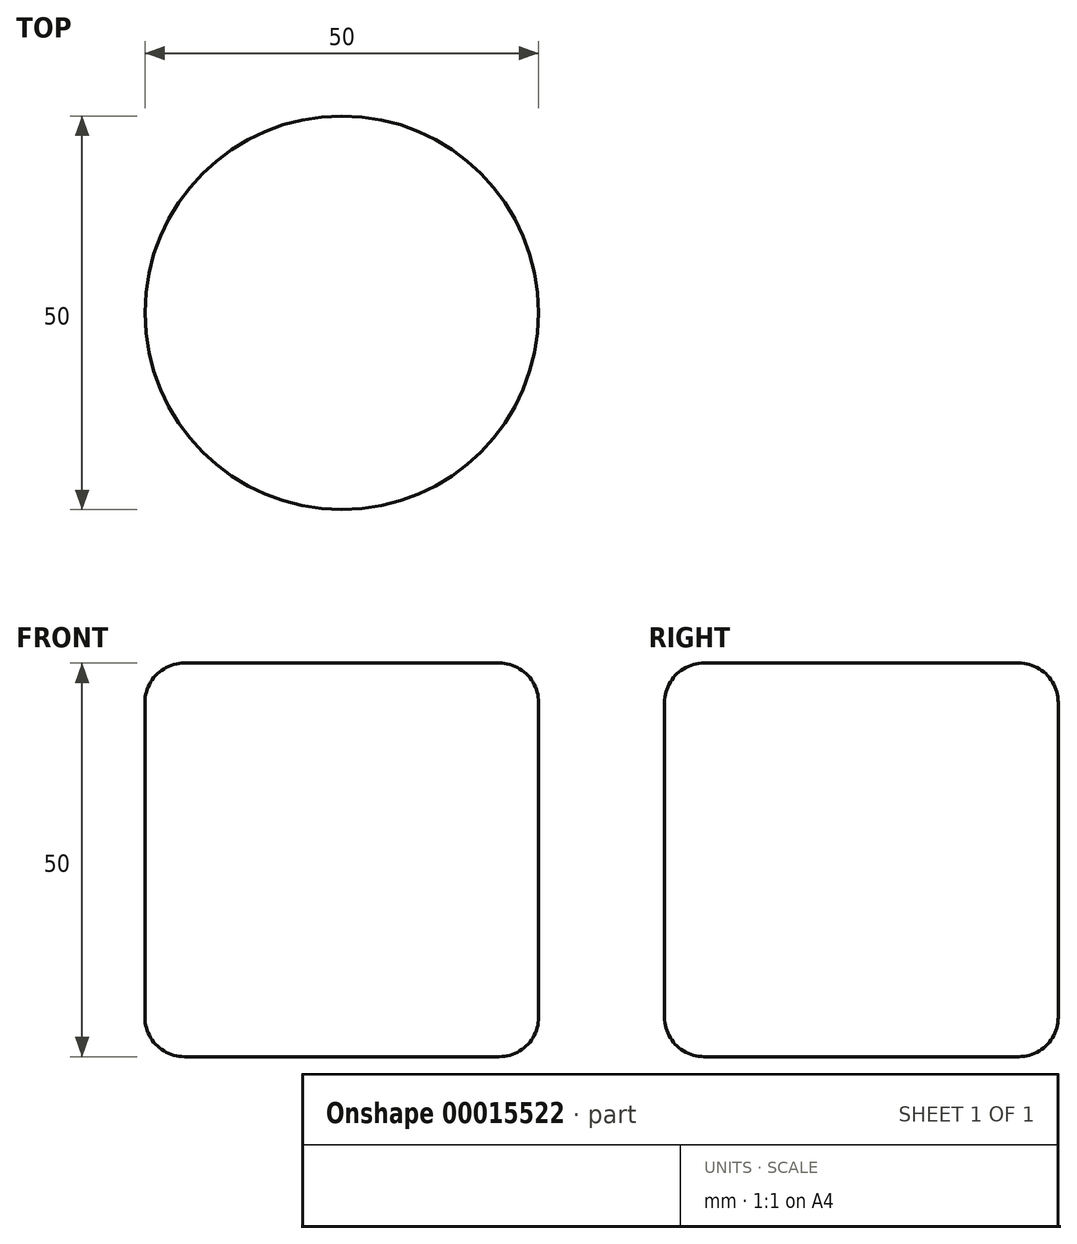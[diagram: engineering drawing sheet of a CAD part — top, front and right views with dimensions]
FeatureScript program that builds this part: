
annotation { "Feature Type Name" : "Feature", "Feature Type Description" : "" }
export const myFeature = defineFeature(function(context is Context, id is Id, definition is map)
    precondition{}
    {
        {
            var Q0;
            Q0=qCreatedBy(makeId("Top.planeOp"),FACE);
            var sketch = newSketch(context, id + "F0", { "sketchPlane" : qUnion([Q0])});
            skCircle(sketch, "E0", {"center": v(0, 0) * mm, "radius": 25 * mm});
            skSolve(sketch);
        }
        {
            var Q0;
            Q0 = qSketchRegion(id + "F0", true);
            extrude(context, id + "F1", {"entities" : qUnion([Q0]), "depth" : 50 * mm});
        }
        {
            var Q0;
            Q0=makeQuery(id+"F1.opExtrude","CAP_FACE",FACE,{"disambiguationData":[OSD([sQuery(id+"F0.wireOp",EDGE,"E0")])],"isStart":false});
            var Q1;
            Q1=makeQuery(id+"F1.opExtrude","CAP_FACE",FACE,{"disambiguationData":[OSD([sQuery(id+"F0.wireOp",EDGE,"E0")])],"isStart":true});
            fillet(context, id + "F2", {"entities" : qUnion([Q0, Q1]), "radius" : 5 * mm, "tangentPropagation" : true, "allowEdgeOverflow" : false});
        }
    });
